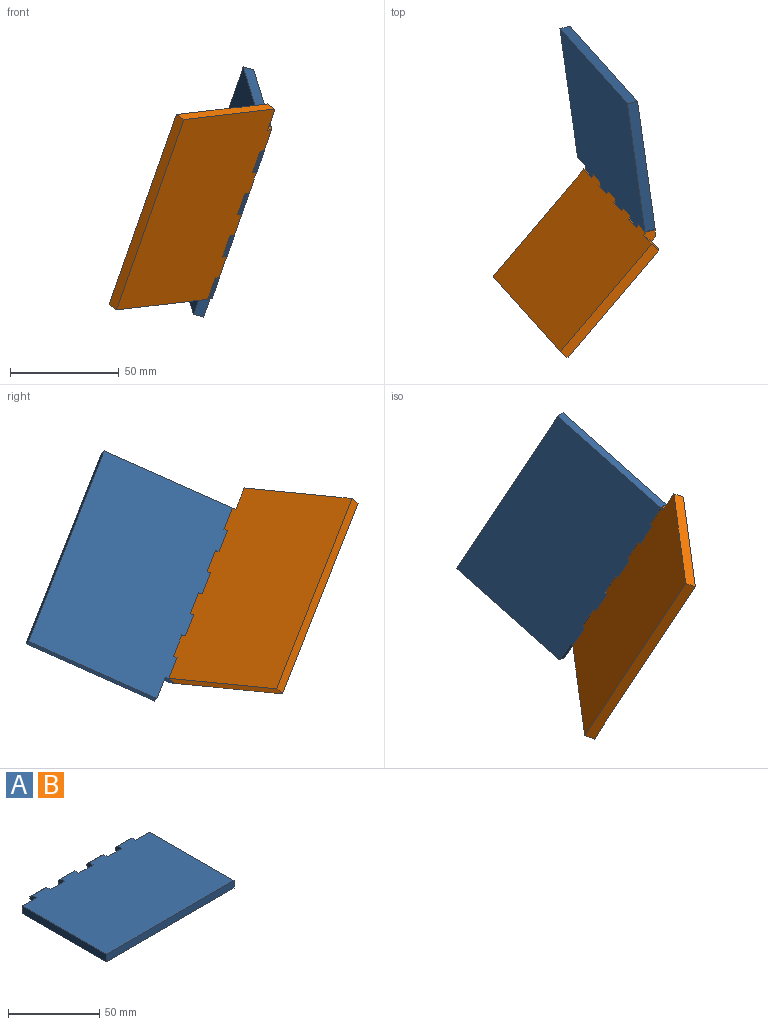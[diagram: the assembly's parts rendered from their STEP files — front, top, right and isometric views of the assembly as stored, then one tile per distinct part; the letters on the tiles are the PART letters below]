
ASSEMBLY  parts=2 mates=1
PART A: 30 faces, bbox 99x70x5 mm
  f0: plane 5x5mm, normal (1,0,0), area 21mm2, adj f1,f19,f20,f21,f24,f27
  f1: plane 11x1mm, normal (0,1,0), area 11mm2, adj f0,f2,f24,f27
  f2: plane 5x5mm, normal (-1,0,0), area 21mm2, adj f1,f3,f20,f21,f24,f27
  f3: plane 11x5mm, normal (0,1,0), area 55mm2, adj f2,f4,f20,f21
  f4: plane 5x5mm, normal (1,0,0), area 21mm2, adj f3,f5,f20,f21,f25,f26
  f5: plane 11x1mm, normal (0,1,0), area 11mm2, adj f4,f6,f25,f26
  f6: plane 5x5mm, normal (-1,0,0), area 21mm2, adj f5,f7,f20,f21,f25,f26
  f7: plane 11x5mm, normal (0,1,0), area 55mm2, adj f6,f8,f20,f21
  f8: plane 65x5mm, normal (-1,0,0), area 325mm2, adj f7,f9,f20,f21
  f9: plane 99x5mm, normal (0,-1,0), area 495mm2, adj f8,f10,f20,f21
  f10: plane 65x5mm, normal (1,0,0), area 325mm2, adj f9,f11,f20,f21
  f11: plane 11x5mm, normal (0,1,0), area 55mm2, adj f10,f12,f20,f21
  f12: plane 5x5mm, normal (1,0,0), area 21mm2, adj f11,f13,f20,f21,f22,f29
  f13: plane 11x1mm, normal (0,1,0), area 11mm2, adj f12,f14,f22,f29
  f14: plane 5x5mm, normal (-1,0,0), area 21mm2, adj f13,f15,f20,f21,f22,f29
  f15: plane 11x5mm, normal (0,1,0), area 55mm2, adj f14,f16,f20,f21
  f16: plane 5x5mm, normal (1,0,0), area 21mm2, adj f15,f17,f20,f21,f23,f28
  f17: plane 11x1mm, normal (0,1,0), area 11mm2, adj f16,f18,f23,f28
  f18: plane 5x5mm, normal (-1,0,0), area 21mm2, adj f17,f19,f20,f21,f23,f28
  f19: plane 11x5mm, normal (0,1,0), area 55mm2, adj f0,f18,f20,f21
  f20: plane 99x68mm, normal (0,0,1), area 6567mm2, adj f0,f2,f3,f4,f6,f7,f8,f9
  f21: plane 99x68mm, normal (0,0,-1), area 6567mm2, adj f0,f2,f3,f4,f6,f7,f8,f9
  f22: plane 11x2mm, normal (0,0.71,-0.71), area 31.1mm2, adj f12,f13,f14,f21
  f23: plane 11x2mm, normal (0,0.71,-0.71), area 31.1mm2, adj f16,f17,f18,f21
  f24: plane 11x2mm, normal (0,0.71,-0.71), area 31.1mm2, adj f0,f1,f2,f21
  f25: plane 11x2mm, normal (0,0.71,-0.71), area 31.1mm2, adj f4,f5,f6,f21
  f26: plane 11x2mm, normal (0,0.71,0.71), area 31.1mm2, adj f4,f5,f6,f20
  f27: plane 11x2mm, normal (0,0.71,0.71), area 31.1mm2, adj f0,f1,f2,f20
  f28: plane 11x2mm, normal (0,0.71,0.71), area 31.1mm2, adj f16,f17,f18,f20
  f29: plane 11x2mm, normal (0,0.71,0.71), area 31.1mm2, adj f12,f13,f14,f20
PART B: same geometry as A
PLACE A rot(axis=(-0.8,0.07,-0.59),156.4deg) t=(46.2,11.92,-35.69)mm
PLACE B rot(axis=(-0.24,-0.82,-0.52),74.4deg) t=(37.09,-46.35,-43.1)mm
MATE revolute B.f14 <-> A.f12  axis (-0.31,0.35,-0.88) through (64.61,-30.11,-15.27)mm
